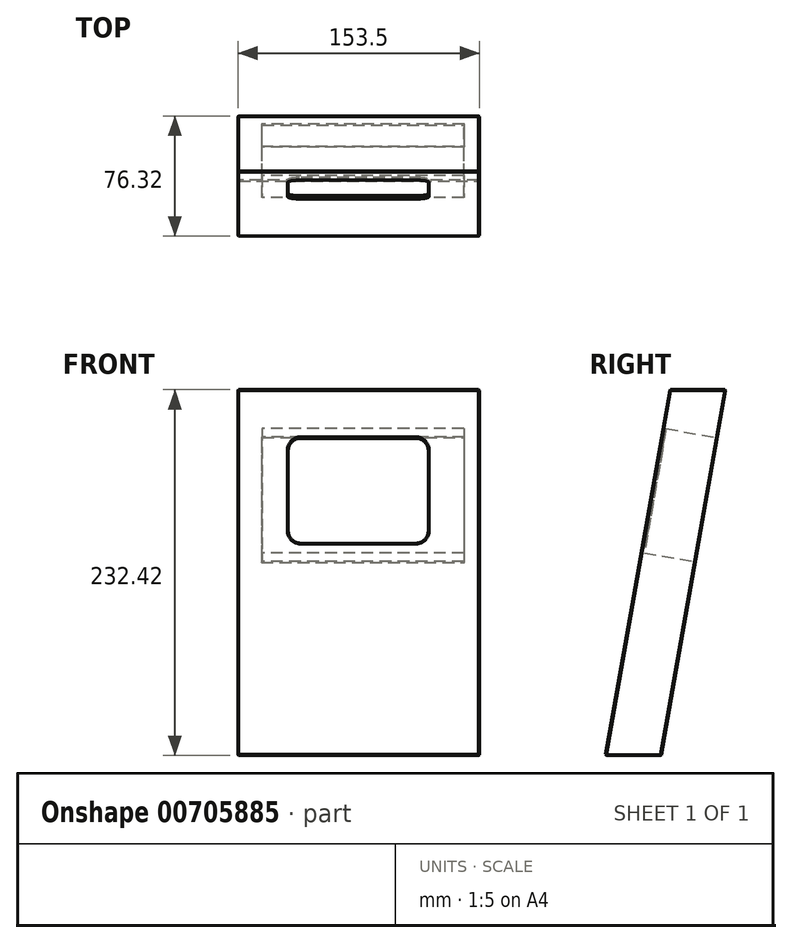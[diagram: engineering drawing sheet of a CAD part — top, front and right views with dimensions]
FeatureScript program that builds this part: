
annotation { "Feature Type Name" : "Feature", "Feature Type Description" : "" }
export const myFeature = defineFeature(function(context is Context, id is Id, definition is map)
    precondition{}
    {
        {
            var Q0;
            Q0=qCreatedBy(makeId("Right.planeOp"),FACE);
            var sketch = newSketch(context, id + "F0", { "sketchPlane" : qUnion([Q0])});
            skLineSegment(sketch, "E0", {"start": v(44.6, 87.86) * mm, "end": v(80.14, 87.86) * mm});
            skLineSegment(sketch, "E1", {"start": v(80.14, 87.86) * mm, "end": v(39.16, -144.56) * mm});
            skLineSegment(sketch, "E2", {"start": v(39.16, -144.56) * mm, "end": v(3.62, -144.56) * mm});
            skLineSegment(sketch, "E3", {"start": v(3.62, -144.56) * mm, "end": v(44.6, 87.86) * mm});
            skSolve(sketch);
        }
        {
            var Q0;
            Q0 = qSketchRegion(id + "F0", true);
            var Q1;
            Q1 = qSketchRegion(id + "F2", true);
            extrude(context, id + "F1", {"entities" : qUnion([Q0, Q1]), "oppositeDirection" : true, "depth" : 153.5 * mm, "offsetDistance" : 25 * mm});
        }
        {
            var Q0;
            Q0=makeQuery(id+"F1.opExtrude","SWEPT_FACE",FACE,{"disambiguationData":[OSD([sQuery(id+"F0.wireOp",EDGE,"E3")])]});
            var sketch = newSketch(context, id + "F2", { "sketchPlane" : qUnion([Q0])});
            skLineSegment(sketch, "E4.bottom", {"start": v(-113.5, 63.27) * mm, "end": v(-40.5, 63.27) * mm});
            skLineSegment(sketch, "E4.top", {"start": v(-113.5, -4.73) * mm, "end": v(-40.5, -4.73) * mm});
            skLineSegment(sketch, "E4.left", {"start": v(-121.5, 55.27) * mm, "end": v(-121.5, 3.27) * mm});
            skLineSegment(sketch, "E4.right", {"start": v(-32.5, 55.27) * mm, "end": v(-32.5, 3.27) * mm});
            skPoint(sketch, "E5.visualSharp", {"position": v(-32.5, 63.27) * mm});
            skArc(sketch, "E5.filletArc", {"start": v(-32.5, 55.27) * mm, "mid": v(-34.84, 60.92) * mm, "end": v(-40.5, 63.27) * mm});
            skPoint(sketch, "E6.visualSharp", {"position": v(-121.5, 63.27) * mm});
            skArc(sketch, "E6.filletArc", {"start": v(-113.5, 63.27) * mm, "mid": v(-119.16, 60.92) * mm, "end": v(-121.5, 55.27) * mm});
            skPoint(sketch, "E7.visualSharp", {"position": v(-121.5, -4.73) * mm});
            skArc(sketch, "E7.filletArc", {"start": v(-121.5, 3.27) * mm, "mid": v(-119.16, -2.4) * mm, "end": v(-113.5, -4.73) * mm});
            skPoint(sketch, "E8.visualSharp", {"position": v(-32.5, -4.73) * mm});
            skArc(sketch, "E8.filletArc", {"start": v(-40.5, -4.73) * mm, "mid": v(-34.84, -2.4) * mm, "end": v(-32.5, 3.27) * mm});
            skSolve(sketch);
        }
        {
            var Q0;
            Q0=makeQuery(id+"F2.imprint","IMPRINT",FACE,{"disambiguationData":[TD([[makeQuery(id+"F2.imprint","IMPRINT",EDGE,{"derivedFrom":sQuery(id+"F2.wireOp",EDGE,"E4.bottom")}),-1.0]])]});
            extrude(context, id + "F3", {"entities" : qUnion([Q0]), "operationType" : NewBodyOperationType.REMOVE, "endBound" : BoundingType.THROUGH_ALL, "oppositeDirection" : true, "depth" : 25 * mm, "offsetDistance" : 25 * mm});
        }
        {
            var Q0;
            Q0=makeQuery(id+"F1.opExtrude","SWEPT_FACE",FACE,{"disambiguationData":[OSD([sQuery(id+"F0.wireOp",EDGE,"E1")])]});
            var sketch = newSketch(context, id + "F4", { "sketchPlane" : qUnion([Q0])});
            skLineSegment(sketch, "E9.bottom", {"start": v(10, 69.44) * mm, "end": v(138, 69.44) * mm});
            skLineSegment(sketch, "E9.top", {"start": v(10, -10.56) * mm, "end": v(138, -10.56) * mm});
            skLineSegment(sketch, "E9.left", {"start": v(10, 69.44) * mm, "end": v(10, -10.56) * mm});
            skLineSegment(sketch, "E9.right", {"start": v(138, 69.44) * mm, "end": v(138, -10.56) * mm});
            skSolve(sketch);
        }
        {
            var Q0;
            Q0 = qSketchRegion(id + "F4", true);
            extrude(context, id + "F5", {"entities" : qUnion([Q0]), "operationType" : NewBodyOperationType.REMOVE, "oppositeDirection" : true, "depth" : 33 * mm, "offsetDistance" : 25 * mm});
        }
        {
            var Q0;
            Q0=makeQuery(id+"F1.opExtrude","SWEPT_FACE",FACE,{"disambiguationData":[OSD([sQuery(id+"F0.wireOp",EDGE,"E3")])]});
            var Q1;
            Q1=makeQuery(id+"F1.opExtrude","CAP_FACE",FACE,{"disambiguationData":[OSD([sQuery(id+"F0.wireOp",EDGE,"E0"),sQuery(id+"F0.wireOp",EDGE,"E1"),sQuery(id+"F0.wireOp",EDGE,"E2"),sQuery(id+"F0.wireOp",EDGE,"E3")])],"isStart":true});
            var Q2;
            Q2=makeQuery(id+"F1.opExtrude","SWEPT_FACE",FACE,{"disambiguationData":[OSD([sQuery(id+"F0.wireOp",EDGE,"E0")])]});
            var Q3;
            Q3=makeQuery(id+"F1.opExtrude","CAP_FACE",FACE,{"disambiguationData":[OSD([sQuery(id+"F0.wireOp",EDGE,"E0"),sQuery(id+"F0.wireOp",EDGE,"E1"),sQuery(id+"F0.wireOp",EDGE,"E2"),sQuery(id+"F0.wireOp",EDGE,"E3")])],"isStart":false});
            var Q4;
            Q4=makeQuery(id+"F1.opExtrude","SWEPT_FACE",FACE,{"disambiguationData":[OSD([sQuery(id+"F0.wireOp",EDGE,"E1")])]});
            chamfer(context, id + "F6", {"entities" : qUnion([Q0, Q1, Q2, Q3, Q4]), "width" : 0.5 * mm, "tangentPropagation" : true});
        }
    });
